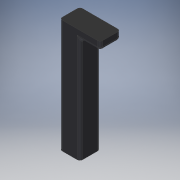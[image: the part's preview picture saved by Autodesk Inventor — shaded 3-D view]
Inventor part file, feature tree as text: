
AUTODESK INVENTOR PART (.ipt)
format: ipt  version: 2018 (Build 220112000, 112)  size: 139,776 bytes
history: native  units: mm
features: other x4, fillet x3, reference x3, sketch x2, extrude x2, plane x1
ambient origin geometry x8: Origin, YZ Plane, XZ Plane, XY Plane, X Axis, Y Axis, Z Axis, Center Point
bodies: Solid1 (feature_tree)
feature tree (15):
  sketch  "Sketch1"  dims[d0=5.0mm d1=7.5mm]
  plane  "Work Plane1"
  extrude  "Extrusion1"  Depth=7.5mm
  extrude  "Extrusion2"  Depth=10.0mm TaperAngle=0.0deg
  fillet  "Fillet1"  Radius=15.0mm
  fillet  "Fillet2"  Radius=3.0mm
  fillet  "Fillet3"  Radius=1.0mm
  reference  "Reference1"
  reference  "Reference2"
  reference  "Reference3"
  sketch  "Sketch2"  dims[d2=7.5mm d3=10.0mm d4=0.0mm d5=15.0mm d6=3.0mm d7=0.0mm d8=1.0mm d9=1.0mm d10=1.0mm]
  other  "<userpath>\OneDrive\Documents\Inventor\TSA\2018\Animatronics\Tortoise\TurtleAssembly2.iam"
  other  "TurtleAssembly2.iam"
  other  "Table:3"
  other  "holder_gear_mount:3"
